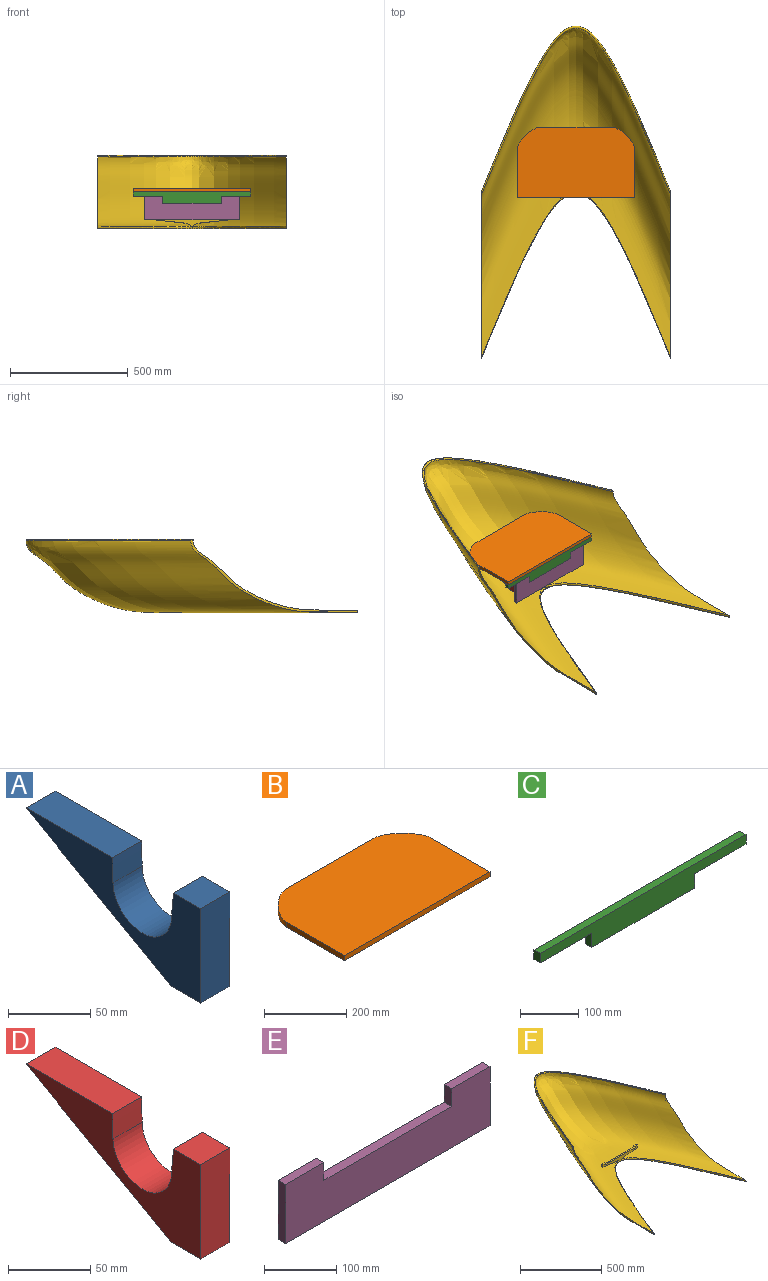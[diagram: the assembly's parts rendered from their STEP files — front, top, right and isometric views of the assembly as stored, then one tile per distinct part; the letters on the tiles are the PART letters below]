
ASSEMBLY  parts=6 mates=5
PART A: 10 faces, bbox 25x150x70 mm
  f0: cylinder r=340.82mm len=25mm, axis (1,0,0), area 493.3mm2, adj f1,f7,f8,f9
  f1: plane 25x23.4mm, normal (0,0,1), area 584.9mm2, adj f0,f2,f8,f9
  f2: plane 70x25mm, normal (0,-1,0), area 1750mm2, adj f1,f3,f8,f9
  f3: plane 25.84x25mm, normal (0,0,-1), area 646.1mm2, adj f2,f4,f8,f9
  f4: plane 124.11x70mm, normal (0,0.49,-0.87), area 3562.2mm2, adj f3,f5,f8,f9
  f5: plane 74.05x25mm, normal (0,0,1), area 1851.1mm2, adj f4,f6,f8,f9
  f6: cylinder r=856.04mm len=25mm, axis (1,0,0), area 462.7mm2, adj f5,f7,f8,f9
  f7: cylinder r=25.12mm len=50.2mm, axis (1,0,0), area 1923.4mm2, adj f0,f6,f8,f9
  f8: plane 149.95x70mm, normal (-1,0,0), area 4234mm2, adj f0,f1,f2,f3,f4,f5,f6,f7
  f9: plane 149.95x70mm, normal (1,0,0), area 4234mm2, adj f0,f1,f2,f3,f4,f5,f6,f7
PART B: 8 faces, bbox 500x300x16.5 mm
  f0: plane 500x300mm, normal (0,0,-1), area 144297.5mm2, adj f1,f3,f4,f5,f6,f7
  f1: plane 200x15mm, normal (1,0,0), area 3000mm2, adj f0,f2,f5,f6
  f2: plane 500x300mm, normal (0,0,1), area 144297.5mm2, adj f1,f3,f4,f5,f6,f7
  f3: plane 200x15mm, normal (-1,0,0), area 3000mm2, adj f0,f2,f5,f7
  f4: plane 300x15mm, normal (0,1,0), area 4500mm2, adj f0,f2,f6,f7
  f5: plane 500x15mm, normal (0,-1,0), area 7500mm2, adj f0,f1,f2,f3
  f6: bspline ~100x100mm, area 2263.4mm2, adj f0,f1,f2,f4
  f7: bspline ~100x100mm, area 2263.4mm2, adj f0,f2,f3,f4
PART C: 10 faces, bbox 500x15x50 mm
  f0: plane 125x15mm, normal (0,0,-1), area 1875mm2, adj f1,f7,f8,f9
  f1: plane 30x15mm, normal (-1,0,0), area 450mm2, adj f0,f2,f8,f9
  f2: plane 250x15mm, normal (0,0,-1), area 3750mm2, adj f1,f3,f8,f9
  f3: plane 30x15mm, normal (1,0,0), area 450mm2, adj f2,f4,f8,f9
  f4: plane 125x15mm, normal (0,0,-1), area 1875mm2, adj f3,f5,f8,f9
  f5: plane 20x15mm, normal (1,0,0), area 300mm2, adj f4,f6,f8,f9
  f6: plane 500x15mm, normal (0,0,1), area 7500mm2, adj f5,f7,f8,f9
  f7: plane 20x15mm, normal (-1,0,0), area 300mm2, adj f0,f6,f8,f9
  f8: plane 500x50mm, normal (0,1,0), area 17500mm2, adj f0,f1,f2,f3,f4,f5,f6,f7
  f9: plane 500x50mm, normal (0,-1,0), area 17500mm2, adj f0,f1,f2,f3,f4,f5,f6,f7
PART D: 10 faces, bbox 25x150x70 mm
  f0: cylinder r=340.82mm len=25mm, axis (-1,0,0), area 493.3mm2, adj f1,f7,f8,f9
  f1: plane 25x23.4mm, normal (0,0,1), area 584.9mm2, adj f0,f2,f8,f9
  f2: plane 70x25mm, normal (0,-1,0), area 1750mm2, adj f1,f3,f8,f9
  f3: plane 25.84x25mm, normal (0,0,-1), area 646.1mm2, adj f2,f4,f8,f9
  f4: plane 124.11x70mm, normal (0,0.49,-0.87), area 3562.2mm2, adj f3,f5,f8,f9
  f5: plane 74.05x25mm, normal (0,0,1), area 1851.1mm2, adj f4,f6,f8,f9
  f6: cylinder r=856.04mm len=25mm, axis (-1,0,0), area 462.7mm2, adj f5,f7,f8,f9
  f7: cylinder r=25.12mm len=50.2mm, axis (-1,0,0), area 1923.4mm2, adj f0,f6,f8,f9
  f8: plane 149.95x70mm, normal (1,0,0), area 4234mm2, adj f0,f1,f2,f3,f4,f5,f6,f7
  f9: plane 149.95x70mm, normal (-1,0,0), area 4234mm2, adj f0,f1,f2,f3,f4,f5,f6,f7
PART E: 10 faces, bbox 400x15x100 mm
  f0: plane 250x15mm, normal (0,0,1), area 3750mm2, adj f1,f7,f8,f9
  f1: plane 30x15mm, normal (1,0,0), area 450mm2, adj f0,f2,f8,f9
  f2: plane 75x15mm, normal (0,0,1), area 1125mm2, adj f1,f3,f8,f9
  f3: plane 100x15mm, normal (-1,0,0), area 1500mm2, adj f2,f4,f8,f9
  f4: plane 400x15mm, normal (0,0,-1), area 6000mm2, adj f3,f5,f8,f9
  f5: plane 100x15mm, normal (1,0,0), area 1500mm2, adj f4,f6,f8,f9
  f6: plane 75x15mm, normal (0,0,1), area 1125mm2, adj f5,f7,f8,f9
  f7: plane 30x15mm, normal (-1,0,0), area 450mm2, adj f0,f6,f8,f9
  f8: plane 400x100mm, normal (0,1,0), area 32500mm2, adj f0,f1,f2,f3,f4,f5,f6,f7
  f9: plane 400x100mm, normal (0,-1,0), area 32500mm2, adj f0,f1,f2,f3,f4,f5,f6,f7
PART F: 18 faces, bbox 800.1x1415.2x316.2 mm
  f0: extruded ~150x30.23mm, area 1533.3mm2, adj f1,f9,f10,f11,f12,f17
  f1: plane 300.13x48.23mm, normal (0,1,0), area 6074.2mm2, adj f0,f2,f3,f4,f5,f6,f7,f8
  f2: plane 20x10mm, normal (1,0,0), area 200mm2, adj f1,f3,f10,f11
  f3: plane 20x10mm, normal (0,0,1), area 200mm2, adj f1,f2,f4,f10
  f4: plane 10x10mm, normal (-1,0,0), area 100mm2, adj f1,f3,f5,f10
  f5: plane 260x10mm, normal (0,0,1), area 2600mm2, adj f1,f4,f6,f10
  f6: plane 10x10mm, normal (1,0,0), area 100mm2, adj f1,f5,f7,f10
  f7: plane 20x10mm, normal (0,0,1), area 200mm2, adj f1,f6,f9,f10
  f8: bspline ~80.76x21.16mm, area 0mm2, adj f1,f17
  f9: plane 20x10mm, normal (-1,0,0), area 200mm2, adj f0,f1,f7,f10
  f10: plane 300x50.23mm, normal (0,-1,0), area 6101.1mm2, adj f0,f2,f3,f4,f5,f6,f7,f9
  f11: extruded ~150x30.23mm, area 1533.3mm2, adj f0,f1,f2,f10,f12,f17
  f12: bspline ~800x710.13mm, area 19869.9mm2, adj f0,f11,f13,f15,f16,f17
  f13: plane 710x311.04mm, normal (1,0,0), area 8155.2mm2, adj f12,f14,f15,f17
  f14: bspline ~800x710mm, area 19924.3mm2, adj f13,f15,f16,f17
  f15: bspline ~1405.06x800mm, area 845072.9mm2, adj f12,f13,f14,f16
  f16: plane 710x311.04mm, normal (-1,0,0), area 8155.2mm2, adj f12,f14,f15,f17
  f17: bspline ~1394.94x800mm, area 825074.8mm2, adj f0,f1,f8,f11,f12,f13,f14,f16
PLACE A at identity
PLACE B at identity
PLACE C at identity
PLACE D at identity
PLACE E at identity fixed
PLACE F t=(0.01,25,199.3)mm
MATE fastened B.f0 <-> C.f6  axis (0,0,-1) through (0,0,50)mm
MATE revolute C.f3 <-> E.f7  axis (1,0,0) through (125,0,0)mm
MATE fastened E.f8 <-> D.f2  axis (0,1,0) through (-200,15,-20)mm
MATE fastened E.f8 <-> A.f2  axis (0,1,0) through (200,15,-20)mm
MATE fastened E.f8 <-> F.f10  axis (0,1,0) through (0,15,-70)mm
